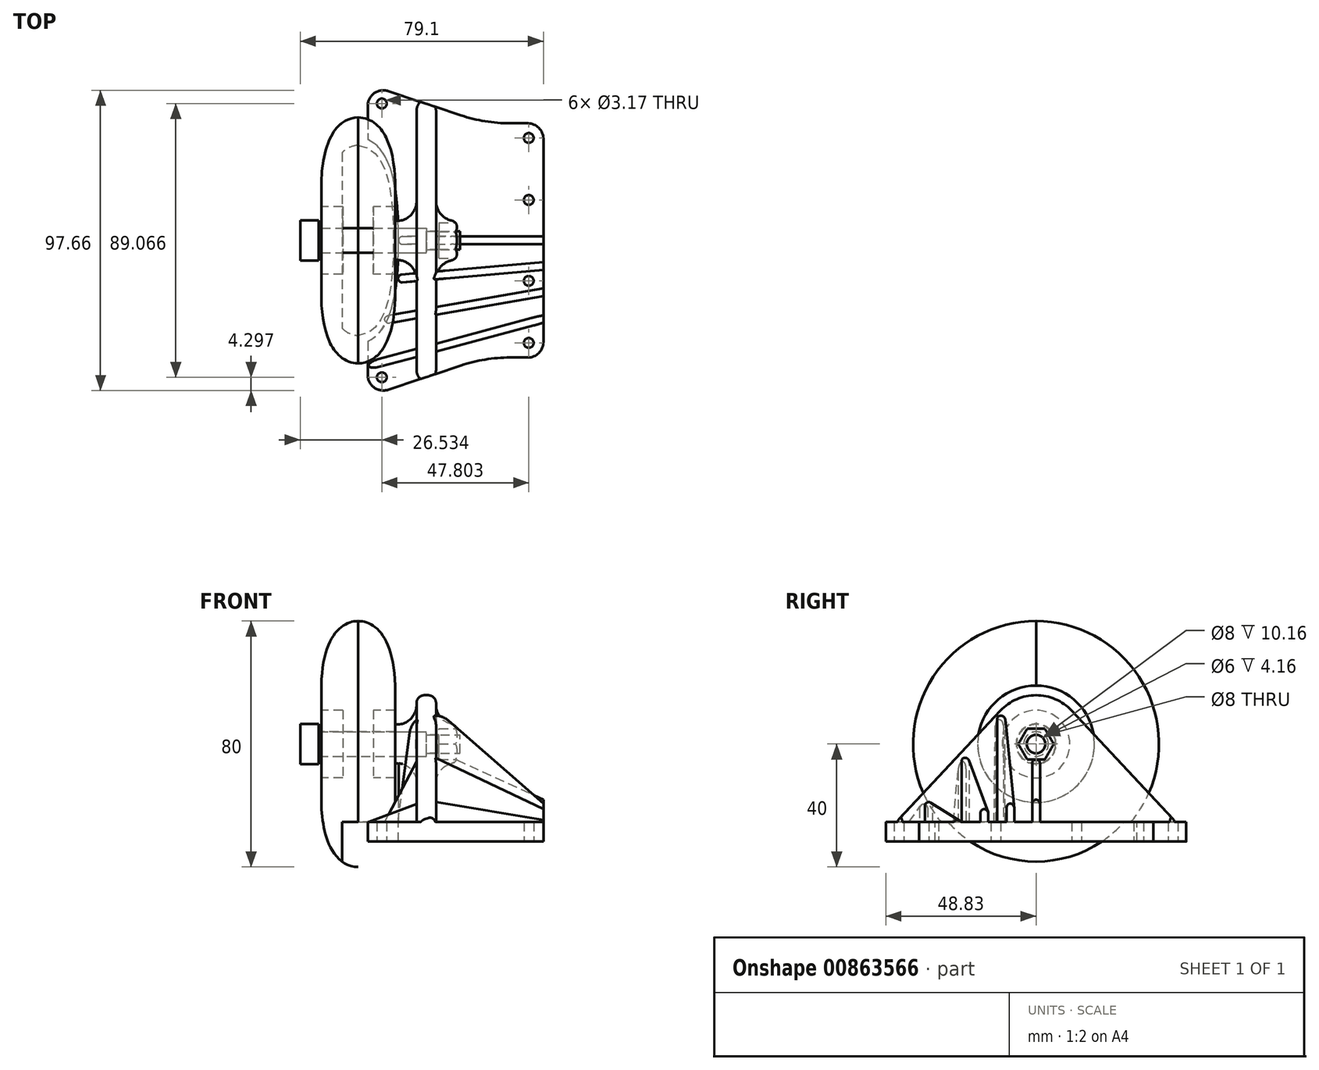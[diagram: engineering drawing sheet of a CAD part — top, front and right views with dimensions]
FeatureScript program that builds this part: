
annotation { "Feature Type Name" : "Feature", "Feature Type Description" : "" }
export const myFeature = defineFeature(function(context is Context, id is Id, definition is map)
    precondition{}
    {
        {
            var Q0;
            Q0=qCreatedBy(makeId("Top.planeOp"),FACE);
            var sketch = newSketch(context, id + "F0", { "sketchPlane" : qUnion([Q0])});
            skLineSegment(sketch, "E0", {"start": v(-19.05, 50.8) * mm, "end": v(-19.05, -50.8) * mm});
            skLineSegment(sketch, "E1", {"start": v(-19.05, -50.8) * mm, "end": v(19.05, -38.1) * mm});
            skLineSegment(sketch, "E2", {"start": v(38.1, -31.75) * mm, "end": v(38.1, 31.75) * mm});
            skLineSegment(sketch, "E3", {"start": v(19.05, 38.1) * mm, "end": v(-19.05, 50.8) * mm});
            skLineSegment(sketch, "E4", {"start": v(19.05, 38.1) * mm, "end": v(38.1, 38.1) * mm});
            skLineSegment(sketch, "E5", {"start": v(38.1, 38.1) * mm, "end": v(38.1, 31.75) * mm});
            skLineSegment(sketch, "E6", {"start": v(19.05, -38.1) * mm, "end": v(38.1, -38.1) * mm});
            skLineSegment(sketch, "E7", {"start": v(38.1, -38.1) * mm, "end": v(38.1, -31.75) * mm});
            skSolve(sketch);
        }
        {
            var Q0;
            Q0=makeQuery(id+"F0.imprint","IMPRINT",FACE,{"disambiguationData":[TD([[makeQuery(id+"F0.imprint","IMPRINT",EDGE,{"derivedFrom":sQuery(id+"F0.wireOp",EDGE,"E0")}),1.0]])]});
            extrude(context, id + "F1", {"entities" : qUnion([Q0]), "depth" : 6.35 * mm});
        }
        {
            var Q0;
            Q0=makeQuery(id+"F1.opExtrude","CAP_FACE",FACE,{"disambiguationData":[OSD([sQuery(id+"F0.wireOp",EDGE,"E0"),sQuery(id+"F0.wireOp",EDGE,"E1"),sQuery(id+"F0.wireOp",EDGE,"E2"),sQuery(id+"F0.wireOp",EDGE,"E3")])],"isStart":false});
            var sketch = newSketch(context, id + "F2", { "sketchPlane" : qUnion([Q0])});
            skLineSegment(sketch, "E8", {"start": v(-3.18, 45.5) * mm, "end": v(-3.17, -45.5) * mm});
            skLineSegment(sketch, "E9", {"start": v(-3.17, -45.5) * mm, "end": v(3.18, -43.4) * mm});
            skLineSegment(sketch, "E10", {"start": v(3.18, -43.4) * mm, "end": v(3.17, 43.4) * mm});
            skLineSegment(sketch, "E11", {"start": v(3.17, 43.4) * mm, "end": v(-3.18, 45.5) * mm});
            skSolve(sketch);
        }
        {
            var Q0;
            Q0=makeQuery(id+"F2.imprint","IMPRINT",FACE,{"disambiguationData":[TD([[makeQuery(id+"F2.imprint","IMPRINT",EDGE,{"derivedFrom":sQuery(id+"F2.wireOp",EDGE,"E8")}),1.0]])]});
            extrude(context, id + "F3", {"entities" : qUnion([Q0]), "operationType" : NewBodyOperationType.ADD, "depth" : 50.8 * mm, "offsetDistance" : 25.4 * mm});
        }
        {
            var Q0;
            Q0=qCreatedBy(makeId("Right.planeOp"),FACE);
            var sketch = newSketch(context, id + "F4", { "sketchPlane" : qUnion([Q0])});
            skArc(sketch, "E12", {"start": v(11.6, 42.6) * mm, "mid": v(0, 47.62) * mm, "end": v(-11.6, 42.6) * mm});
            skLineSegment(sketch, "E13", {"start": v(11.6, 42.6) * mm, "end": v(45.5, 6.35) * mm});
            skLineSegment(sketch, "E14", {"start": v(-11.6, 42.6) * mm, "end": v(-45.5, 6.35) * mm});
            skLineSegment(sketch, "E15", {"start": v(45.5, 6.35) * mm, "end": v(53.44, 6.35) * mm});
            skLineSegment(sketch, "E16", {"start": v(53.44, 6.35) * mm, "end": v(53.44, 59.99) * mm});
            skLineSegment(sketch, "E17", {"start": v(53.44, 59.99) * mm, "end": v(-55.67, 59.99) * mm});
            skLineSegment(sketch, "E18", {"start": v(-55.67, 59.99) * mm, "end": v(-55.67, 6.35) * mm});
            skLineSegment(sketch, "E19", {"start": v(-55.67, 6.35) * mm, "end": v(-45.5, 6.35) * mm});
            skSolve(sketch);
        }
        {
            var Q0;
            Q0=makeQuery(id+"F4.imprint","IMPRINT",FACE,{"disambiguationData":[TD([[makeQuery(id+"F4.imprint","IMPRINT",EDGE,{"derivedFrom":sQuery(id+"F4.wireOp",EDGE,"E12")}),-1.0]])]});
            extrude(context, id + "F5", {"entities" : qUnion([Q0]), "operationType" : NewBodyOperationType.REMOVE, "oppositeDirection" : true, "depth" : 7.11 * mm, "hasSecondDirection" : true, "secondDirectionOppositeDirection" : false, "secondDirectionDepth" : 4.06 * mm});
        }
        {
            var Q0;
            Q0=qCreatedBy(makeId("Right.planeOp"),FACE);
            var sketch = newSketch(context, id + "F6", { "sketchPlane" : qUnion([Q0])});
            skCircle(sketch, "E20", {"center": v(0, 513) * mm, "radius": 63.5 * mm});
            skCircle(sketch, "E21", {"center": v(0, 31.75) * mm, "radius": 6.35 * mm});
            skSolve(sketch);
        }
        {
            var Q0;
            Q0=qSketchRegion(id+"F6",true);
            extrude(context, id + "F7", {"entities" : qUnion([Q0]), "operationType" : NewBodyOperationType.ADD, "depth" : 10.16 * mm, "hasSecondDirection" : true, "secondDirectionOppositeDirection" : true, "secondDirectionDepth" : 10.16 * mm});
        }
        {
            var Q0;
            Q0=makeQuery(id+"F7.boolean.opBoolean","INTERSECT",EDGE,{"derivedFrom":[makeQuery(id+"F3.opExtrude","SWEPT_FACE",FACE,{"disambiguationData":[OSD([sQuery(id+"F2.wireOp",EDGE,"E8")])]}),makeQuery(id+"F7.opExtrude","SWEPT_FACE",FACE,{"disambiguationData":[OSD([sQuery(id+"F6.wireOp",EDGE,"E21")])]})]});
            var Q1;
            Q1=makeQuery(id+"F7.boolean.opBoolean","INTERSECT",EDGE,{"derivedFrom":[makeQuery(id+"F3.opExtrude","SWEPT_FACE",FACE,{"disambiguationData":[OSD([sQuery(id+"F2.wireOp",EDGE,"E10")])]}),makeQuery(id+"F7.opExtrude","SWEPT_FACE",FACE,{"disambiguationData":[OSD([sQuery(id+"F6.wireOp",EDGE,"E21")])]})]});
            fillet(context, id + "F8", {"entities" : qUnion([Q0, Q1]), "radius" : 6.35 * mm, "tangentPropagation" : true, "allowEdgeOverflow" : false});
        }
        {
            var Q0;
            Q0=makeQuery(id+"F5.boolean.opBoolean","INTERSECT",EDGE,{"derivedFrom":[makeQuery(id+"F3.opExtrude","SWEPT_FACE",FACE,{"disambiguationData":[OSD([sQuery(id+"F2.wireOp",EDGE,"E8")])]}),makeQuery(id+"F5.opExtrude","SWEPT_FACE",FACE,{"disambiguationData":[OSD([sQuery(id+"F4.wireOp",EDGE,"E13")])]})]});
            var Q1;
            Q1=makeQuery(id+"F5.boolean.opBoolean","INTERSECT",EDGE,{"derivedFrom":[makeQuery(id+"F3.opExtrude","SWEPT_FACE",FACE,{"disambiguationData":[OSD([sQuery(id+"F2.wireOp",EDGE,"E10")])]}),makeQuery(id+"F5.opExtrude","SWEPT_FACE",FACE,{"disambiguationData":[OSD([sQuery(id+"F4.wireOp",EDGE,"E13")])]})]});
            fillet(context, id + "F9", {"entities" : qUnion([Q0, Q1]), "radius" : 2.54 * mm, "tangentPropagation" : true, "allowEdgeOverflow" : false});
        }
        {
            var Q0;
            Q0=qCreatedBy(makeId("Right.planeOp"),FACE);
            var sketch = newSketch(context, id + "F10", { "sketchPlane" : qUnion([Q0])});
            skCircle(sketch, "E22", {"center": v(0, 31.75) * mm, "radius": 4 * mm});
            skSolve(sketch);
        }
        {
            var Q0;
            Q0=qSketchRegion(id+"F10",true);
            extrude(context, id + "F11", {"entities" : qUnion([Q0]), "operationType" : NewBodyOperationType.REMOVE, "oppositeDirection" : true, "depth" : 25.4 * mm});
        }
        {
            var Q0;
            Q0=makeQuery(id+"F7.opExtrude","CAP_FACE",FACE,{"disambiguationData":[OSD([sQuery(id+"F6.wireOp",EDGE,"E21")])],"isStart":false});
            var sketch = newSketch(context, id + "F12", { "sketchPlane" : qUnion([Q0])});
            skCircle(sketch, "E23.cCircle", {"center": v(0, 31.75) * mm, "radius": 5 * mm, "construction": true});
            skLineSegment(sketch, "E23.0", {"start": v(-2.89, 36.75) * mm, "end": v(2.89, 36.75) * mm});
            skLineSegment(sketch, "E23.1", {"start": v(2.89, 36.75) * mm, "end": v(5.77, 31.75) * mm});
            skLineSegment(sketch, "E23.2", {"start": v(5.77, 31.75) * mm, "end": v(2.89, 26.75) * mm});
            skLineSegment(sketch, "E23.3", {"start": v(2.89, 26.75) * mm, "end": v(-2.89, 26.75) * mm});
            skLineSegment(sketch, "E23.4", {"start": v(-2.89, 26.75) * mm, "end": v(-5.77, 31.75) * mm});
            skLineSegment(sketch, "E23.5", {"start": v(-5.77, 31.75) * mm, "end": v(-2.89, 36.75) * mm});
            skPoint(sketch, "E23.0.midPoint", {"position": v(0, 36.75) * mm});
            skSolve(sketch);
        }
        {
            var Q0;
            Q0=makeQuery(id+"F12.imprint","IMPRINT",FACE,{"disambiguationData":[TD([[makeQuery(id+"F12.imprint","IMPRINT",EDGE,{"derivedFrom":sQuery(id+"F12.wireOp",EDGE,"E23.0")}),-1.0]])]});
            extrude(context, id + "F13", {"entities" : qUnion([Q0]), "operationType" : NewBodyOperationType.REMOVE, "oppositeDirection" : true, "depth" : 6 * mm});
        }
        {
            var Q0;
            Q0=makeQuery(id+"F7.opExtrude","CAP_EDGE",EDGE,{"disambiguationData":[OSD([sQuery(id+"F6.wireOp",EDGE,"E21")])],"isStart":false});
            fillet(context, id + "F14", {"entities" : qUnion([Q0]), "radius" : 2.54 * mm, "tangentPropagation" : true, "allowEdgeOverflow" : false});
        }
        {
            var Q0;
            Q0=makeQuery(id+"F7.opExtrude","SWEPT_BODY",BODY,{"disambiguationData":[OSD([sQuery(id+"F6.wireOp",EDGE,"E20")])]});
            deleteBodies(context, id + "F15", {"entities" : qUnion([Q0])});
        }
        {
            var Q0;
            Q0=qCreatedBy(makeId("Right.planeOp"),FACE);
            var sketch = newSketch(context, id + "F16", { "sketchPlane" : qUnion([Q0])});
            skCircle(sketch, "E24", {"center": v(0, 31.75) * mm, "radius": 3 * mm});
            skSolve(sketch);
        }
        {
            var Q0;
            Q0=qSketchRegion(id+"F16",true);
            extrude(context, id + "F17", {"entities" : qUnion([Q0]), "operationType" : NewBodyOperationType.REMOVE, "depth" : 25.4 * mm});
        }
        {
            var Q0;
            Q0=qCreatedBy(makeId("Front.planeOp"),FACE);
            var sketch = newSketch(context, id + "F18", { "sketchPlane" : qUnion([Q0])});
            skLineSegment(sketch, "E25", {"start": v(0, 31.75) * mm, "end": v(-46.53, 31.75) * mm, "construction": true});
            skLineSegment(sketch, "E26", {"start": v(-35, 35.75) * mm, "end": v(0, 35.75) * mm});
            skLineSegment(sketch, "E27", {"start": v(0, 35.75) * mm, "end": v(0, 34.75) * mm});
            skLineSegment(sketch, "E28", {"start": v(0, 34.75) * mm, "end": v(11, 34.75) * mm});
            skLineSegment(sketch, "E29", {"start": v(11, 34.75) * mm, "end": v(11, 31.75) * mm});
            skLineSegment(sketch, "E30", {"start": v(11, 31.75) * mm, "end": v(-41, 31.75) * mm});
            skLineSegment(sketch, "E31", {"start": v(-35, 35.75) * mm, "end": v(-35, 38.25) * mm});
            skLineSegment(sketch, "E32", {"start": v(-35, 38.25) * mm, "end": v(-41, 38.25) * mm});
            skLineSegment(sketch, "E33", {"start": v(-41, 38.25) * mm, "end": v(-41, 31.75) * mm});
            skSolve(sketch);
        }
        {
            var Q0;
            Q0=makeQuery(id+"F18.imprint","IMPRINT",FACE,{"disambiguationData":[TD([[makeQuery(id+"F18.imprint","IMPRINT",EDGE,{"derivedFrom":sQuery(id+"F18.wireOp",EDGE,"E26")}),-1.0]])]});
            var Q1;
            Q1=sQuery(id+"F18.wireOp",EDGE,"E25");
            revolve(context, id + "F19", {"entities" : qUnion([Q0]), "axis" : qUnion([Q1]), "revolveType" : RevolveType.FULL});
        }
        {
            var Q0;
            Q0=qCreatedBy(makeId("Front.planeOp"),FACE);
            var sketch = newSketch(context, id + "F20", { "sketchPlane" : qUnion([Q0])});
            skLineSegment(sketch, "E34", {"start": v(-51.26, 31.75) * mm, "end": v(0, 31.75) * mm});
            skLineSegment(sketch, "E35", {"start": v(-22.16, 31.75) * mm, "end": v(-22.16, 71.75) * mm, "construction": true});
            skPoint(sketch, "E36", {"position": v(-25.63, 31.75) * mm});
            skLineSegment(sketch, "E37", {"start": v(-22.16, 35.75) * mm, "end": v(-10.16, 35.75) * mm});
            skLineSegment(sketch, "E38", {"start": v(-10.16, 35.75) * mm, "end": v(-10.16, 50.75) * mm});
            skPoint(sketch, "E39.MirrorCS.2.internal.orphan", {"position": v(-34.16, 31.75) * mm});
            skPoint(sketch, "E39.MirrorCS.start.orphan", {"position": v(-22.16, 71.75) * mm});
            skPoint(sketch, "E40.2.internal.orphan", {"position": v(-10.16, 31.75) * mm});
            skFitSpline(sketch, "E41", {"points": [v(-22.16, 71.75) * mm, v(-10.16, 50.75) * mm], "startDerivative": vector(15.26, -0.07) * mm, "endDerivative": vector(1.21, -49.43) * mm});
            skPoint(sketch, "E42.MirrorCS.end.orphan", {"position": v(-34.16, 50.75) * mm});
            skFitSpline(sketch, "E43.MirrorCS", {"points": [v(-22.16, 71.75) * mm, v(-34.16, 50.75) * mm], "startDerivative": vector(-15.26, -0.07) * mm, "endDerivative": vector(-1.21, -49.43) * mm});
            skLineSegment(sketch, "E44.MirrorCS", {"start": v(-34.16, 35.75) * mm, "end": v(-34.16, 50.75) * mm});
            skLineSegment(sketch, "E45.MirrorCS", {"start": v(-22.16, 35.75) * mm, "end": v(-34.16, 35.75) * mm});
            skSolve(sketch);
        }
        {
            var Q0;
            Q0=makeQuery(id+"F20.imprint","IMPRINT",FACE,{"disambiguationData":[TD([[makeQuery(id+"F20.imprint","IMPRINT",EDGE,{"derivedFrom":sQuery(id+"F20.wireOp",EDGE,"E37")}),1.0]])]});
            var Q1;
            Q1=sQuery(id+"F20.wireOp",EDGE,"E34");
            revolve(context, id + "F21", {"entities" : qUnion([Q0]), "axis" : qUnion([Q1]), "revolveType" : RevolveType.FULL});
        }
        {
            var Q0;
            Q0=qCreatedBy(makeId("Front.planeOp"),FACE);
            var sketch = newSketch(context, id + "F22", { "sketchPlane" : qUnion([Q0])});
            skLineSegment(sketch, "E46", {"start": v(-62.06, 31.75) * mm, "end": v(0, 31.75) * mm, "construction": true});
            skLineSegment(sketch, "E47", {"start": v(-10.16, 31.75) * mm, "end": v(-10.16, 42.75) * mm});
            skLineSegment(sketch, "E48", {"start": v(-10.16, 42.75) * mm, "end": v(-17.16, 42.75) * mm});
            skLineSegment(sketch, "E49", {"start": v(-17.16, 42.75) * mm, "end": v(-17.16, 31.75) * mm});
            skLineSegment(sketch, "E50", {"start": v(-17.16, 31.75) * mm, "end": v(-10.16, 31.75) * mm});
            skLineSegment(sketch, "E51", {"start": v(-22.16, 31.75) * mm, "end": v(-22.16, 46.12) * mm, "construction": true});
            skLineSegment(sketch, "E52.MirrorCS", {"start": v(-34.16, 42.75) * mm, "end": v(-27.16, 42.75) * mm});
            skLineSegment(sketch, "E53.MirrorCS", {"start": v(-27.16, 42.75) * mm, "end": v(-27.16, 31.75) * mm});
            skLineSegment(sketch, "E54.MirrorCS", {"start": v(-34.16, 31.75) * mm, "end": v(-34.16, 42.75) * mm});
            skLineSegment(sketch, "E55", {"start": v(-27.16, 31.75) * mm, "end": v(-34.16, 31.75) * mm});
            skSolve(sketch);
        }
        {
            var Q0;
            Q0=qSketchRegion(id+"F22",true);
            var Q1;
            Q1=sQuery(id+"F22.wireOp",EDGE,"E46");
            revolve(context, id + "F23", {"entities" : qUnion([Q0]), "axis" : qUnion([Q1]), "revolveType" : RevolveType.FULL});
        }
        {
            var Q0;
            {var subQ0=sQuery(id+"F0.wireOp",EDGE,"E3");var subQ1=sQuery(id+"F0.wireOp",EDGE,"E1");var subQ2=sQuery(id+"F0.wireOp",EDGE,"E0");Q0=makeQuery(id+"F3.boolean.opBoolean","SPLIT",FACE,{"disambiguationData":[TD([makeQuery(id+"F1.opExtrude","SWEPT_FACE",FACE,{"disambiguationData":[OSD([subQ2])]})])],"derivedFrom":makeQuery(id+"F1.opExtrude","CAP_FACE",FACE,{"disambiguationData":[OSD([subQ2,subQ1,sQuery(id+"F0.wireOp",EDGE,"E2"),subQ0])],"isStart":false})});}
            var sketch = newSketch(context, id + "F24", { "sketchPlane" : qUnion([Q0])});
            skLineSegment(sketch, "E56", {"start": v(-19.05, 32.85) * mm, "end": v(-19.05, -32.85) * mm});
            skFitSpline(sketch, "E57.0", {"points": [v(-22.67, -33.39) * mm, v(-22.46, -33.43) * mm, v(-22.05, -33.49) * mm, v(-21.48, -33.49) * mm, v(-20.97, -33.44) * mm, v(-20.5, -33.35) * mm, v(-20.07, -33.24) * mm, v(-19.65, -33.1) * mm, v(-19.27, -32.95) * mm, v(-18.9, -32.79) * mm, v(-18.56, -32.62) * mm, v(-18.23, -32.43) * mm, v(-17.91, -32.24) * mm, v(-17.5, -31.97) * mm, v(-17.03, -31.62) * mm, v(-16.3, -31.03) * mm, v(-15.49, -30.22) * mm, v(-14.62, -29.2) * mm, v(-13.87, -28.1) * mm, v(-13.21, -26.98) * mm, v(-12.65, -25.84) * mm, v(-12.17, -24.7) * mm, v(-11.76, -23.55) * mm, v(-11.28, -22.02) * mm, v(-10.8, -20.12) * mm, v(-10.34, -17.83) * mm, v(-10, -15.56) * mm, v(-9.63, -12.57) * mm, v(-9.33, -8.85) * mm, v(-9.13, -4.4) * mm, v(-9.07, 0.02) * mm, v(-9.13, 4.46) * mm, v(-9.3, 8.17) * mm, v(-9.52, 11.16) * mm, v(-9.73, 13.4) * mm, v(-10, 15.66) * mm, v(-10.36, 17.92) * mm, v(-10.81, 20.2) * mm, v(-11.4, 22.47) * mm, v(-12.03, 24.37) * mm, v(-12.67, 25.89) * mm, v(-13.24, 27.03) * mm, v(-13.9, 28.15) * mm, v(-14.65, 29.23) * mm, v(-15.52, 30.26) * mm, v(-16.5, 31.2) * mm, v(-17.6, 32.06) * mm, v(-18.66, 32.7) * mm, v(-19.65, 33.11) * mm, v(-20.35, 33.32) * mm, v(-20.98, 33.44) * mm, v(-21.49, 33.49) * mm, v(-22.05, 33.48) * mm, v(-22.46, 33.43) * mm, v(-22.67, 33.39) * mm]});
            skPoint(sketch, "E58.trimOffspring.end.orphan", {"position": v(-22.16, 30.9) * mm});
            skPoint(sketch, "E59.start.orphan", {"position": v(-22.16, -30.9) * mm});
            skLineSegment(sketch, "E60", {"start": v(-19.05, 32.85) * mm, "end": v(-27.36, 32.85) * mm});
            skLineSegment(sketch, "E61", {"start": v(-27.36, 32.85) * mm, "end": v(-27.36, -33.81) * mm});
            skLineSegment(sketch, "E62", {"start": v(-27.36, -33.81) * mm, "end": v(-19.05, -32.85) * mm});
            skSolve(sketch);
        }
        {
            var Q0;
            Q0=makeQuery(id+"F24.imprint","IMPRINT",FACE,{"disambiguationData":[TD([[makeQuery(id+"F24.imprint","IMPRINT",EDGE,{"derivedFrom":sQuery(id+"F24.wireOp",EDGE,"E56")}),-1.0]])]});
            var Q1;
            Q1=makeQuery(id+"F24.imprint","IMPRINT",FACE,{"disambiguationData":[TD([[makeQuery(id+"F24.imprint","IMPRINT",EDGE,{"derivedFrom":sQuery(id+"F24.wireOp",EDGE,"E56")}),1.0]])]});
            extrude(context, id + "F25", {"entities" : qUnion([Q0, Q1]), "operationType" : NewBodyOperationType.REMOVE, "oppositeDirection" : true, "depth" : 25.4 * mm});
        }
        {
            var Q0;
            Q0=qCreatedBy(makeId("Front.planeOp"),FACE);
            var sketch = newSketch(context, id + "F26", { "sketchPlane" : qUnion([Q0])});
            skLineSegment(sketch, "E63", {"start": v(-9.01, 6.35) * mm, "end": v(-9.01, 26.67) * mm});
            skLineSegment(sketch, "E64", {"start": v(-9.01, 26.67) * mm, "end": v(9.85, 26.67) * mm});
            skLineSegment(sketch, "E65", {"start": v(9.85, 26.67) * mm, "end": v(53.98, 6.35) * mm});
            skLineSegment(sketch, "E66", {"start": v(53.98, 6.35) * mm, "end": v(-9.01, 6.35) * mm});
            skSolve(sketch);
        }
        {
            var Q0;
            Q0=makeQuery(id+"F26.imprint","IMPRINT",FACE,{"disambiguationData":[TD([[makeQuery(id+"F26.imprint","IMPRINT",EDGE,{"derivedFrom":sQuery(id+"F26.wireOp",EDGE,"E63")}),-1.0]])]});
            extrude(context, id + "F27", {"entities" : qUnion([Q0]), "operationType" : NewBodyOperationType.ADD, "depth" : 1.27 * mm, "hasSecondDirection" : true, "secondDirectionOppositeDirection" : true, "secondDirectionDepth" : 1.27 * mm});
        }
        {
            var Q0;
            Q0=qCreatedBy(makeId("Top.planeOp"),FACE);
            var sketch = newSketch(context, id + "F28", { "sketchPlane" : qUnion([Q0])});
            skLineSegment(sketch, "E67", {"start": v(-23.06, -52.14) * mm, "end": v(133.35, 0) * mm});
            skLineSegment(sketch, "E68", {"start": v(133.35, 0) * mm, "end": v(-28.84, 0) * mm});
            skLineSegment(sketch, "E69", {"start": v(133.35, 0) * mm, "end": v(-37.86, -14.98) * mm});
            skLineSegment(sketch, "E70", {"start": v(133.35, 0) * mm, "end": v(-37.54, -30.13) * mm});
            skLineSegment(sketch, "E71", {"start": v(133.35, 0) * mm, "end": v(-45.99, -48.05) * mm});
            skSolve(sketch);
        }
        {
            var Q0;
            Q0=sQuery(id+"F28.wireOp",EDGE,"E69");
            cPlane(context, id + "F29", {"entities" : qUnion([Q0]), "cplaneType" : CPlaneType.LINE_ANGLE, "offset" : 25.4 * mm, "angle" : 0 * degree, "width" : 152.4 * mm, "height" : 152.4 * mm});
        }
        {
            var Q0;
            Q0=qCreatedBy(id+"F29.planeOp",FACE);
            var sketch = newSketch(context, id + "F30", { "sketchPlane" : qUnion([Q0])});
            skLineSegment(sketch, "E72", {"start": v(6.12, 39.44) * mm, "end": v(44.18, 6.35) * mm});
            skLineSegment(sketch, "E73", {"start": v(44.18, 6.35) * mm, "end": v(-10.24, 6.35) * mm});
            skLineSegment(sketch, "E74", {"start": v(-10.24, 6.35) * mm, "end": v(-6.43, 35.5) * mm});
            skPoint(sketch, "E75.visualSharp", {"position": v(-6.52, 34.82) * mm});
            skArc(sketch, "E75.filletArc", {"start": v(-3.16, 40.25) * mm, "mid": v(-5.37, 38.27) * mm, "end": v(-6.43, 35.5) * mm});
            skLineSegment(sketch, "E76", {"start": v(1.95, 41) * mm, "end": v(0.46, 41) * mm});
            skLineSegment(sketch, "E77", {"start": v(0.46, 41) * mm, "end": v(-3.16, 40.25) * mm});
            skPoint(sketch, "E78.visualSharp", {"position": v(4.32, 41) * mm});
            skArc(sketch, "E78.filletArc", {"start": v(6.12, 39.44) * mm, "mid": v(4.17, 40.6) * mm, "end": v(1.95, 41) * mm});
            skSolve(sketch);
        }
        {
            var Q0;
            Q0=makeQuery(id+"F30.imprint","IMPRINT",FACE,{"disambiguationData":[TD([[makeQuery(id+"F30.imprint","IMPRINT",EDGE,{"derivedFrom":sQuery(id+"F30.wireOp",EDGE,"E72")}),-1.0]])]});
            extrude(context, id + "F31", {"entities" : qUnion([Q0]), "operationType" : NewBodyOperationType.ADD, "depth" : 1.27 * mm, "hasSecondDirection" : true, "secondDirectionOppositeDirection" : true, "secondDirectionDepth" : 1.27 * mm});
        }
        {
            var Q0;
            Q0=sQuery(id+"F28.wireOp",EDGE,"E70");
            cPlane(context, id + "F32", {"entities" : qUnion([Q0]), "cplaneType" : CPlaneType.LINE_ANGLE, "offset" : 25.4 * mm, "angle" : 0 * degree, "width" : 152.4 * mm, "height" : 152.4 * mm});
        }
        {
            var Q0;
            Q0=qCreatedBy(id+"F32.planeOp",FACE);
            var sketch = newSketch(context, id + "F33", { "sketchPlane" : qUnion([Q0])});
            skLineSegment(sketch, "E79", {"start": v(43.53, 6.35) * mm, "end": v(-17.77, 6.35) * mm});
            skLineSegment(sketch, "E80", {"start": v(-17.77, 6.35) * mm, "end": v(-6.14, 28.2) * mm});
            skLineSegment(sketch, "E81", {"start": v(-6.14, 28.2) * mm, "end": v(-2.9, 28.2) * mm});
            skLineSegment(sketch, "E82", {"start": v(-2.9, 28.2) * mm, "end": v(43.53, 6.35) * mm});
            skSolve(sketch);
        }
        {
            var Q0;
            Q0=makeQuery(id+"F33.imprint","IMPRINT",FACE,{"disambiguationData":[TD([[makeQuery(id+"F33.imprint","IMPRINT",EDGE,{"derivedFrom":sQuery(id+"F33.wireOp",EDGE,"E79")}),-1.0]])]});
            extrude(context, id + "F34", {"entities" : qUnion([Q0]), "operationType" : NewBodyOperationType.ADD, "depth" : 1.27 * mm, "hasSecondDirection" : true, "secondDirectionOppositeDirection" : true, "secondDirectionDepth" : 1.27 * mm});
        }
        {
            var Q0;
            Q0=sQuery(id+"F28.wireOp",EDGE,"E71");
            cPlane(context, id + "F35", {"entities" : qUnion([Q0]), "cplaneType" : CPlaneType.LINE_ANGLE, "offset" : 25.4 * mm, "angle" : 0 * degree, "width" : 152.4 * mm, "height" : 152.4 * mm});
        }
        {
            var Q0;
            Q0=qCreatedBy(id+"F35.planeOp",FACE);
            var sketch = newSketch(context, id + "F36", { "sketchPlane" : qUnion([Q0])});
            skLineSegment(sketch, "E83", {"start": v(-28.7, 6.35) * mm, "end": v(-10.05, 13.08) * mm});
            skLineSegment(sketch, "E84", {"start": v(-10.05, 13.08) * mm, "end": v(-7.43, 13.08) * mm});
            skLineSegment(sketch, "E85", {"start": v(-7.43, 13.08) * mm, "end": v(34.6, 6.35) * mm});
            skLineSegment(sketch, "E86", {"start": v(34.6, 6.35) * mm, "end": v(-28.7, 6.35) * mm});
            skSolve(sketch);
        }
        {
            var Q0;
            Q0=makeQuery(id+"F36.imprint","IMPRINT",FACE,{"disambiguationData":[TD([[makeQuery(id+"F36.imprint","IMPRINT",EDGE,{"derivedFrom":sQuery(id+"F36.wireOp",EDGE,"E83")}),-1.0]])]});
            extrude(context, id + "F37", {"entities" : qUnion([Q0]), "operationType" : NewBodyOperationType.ADD, "depth" : 1.27 * mm, "hasSecondDirection" : true, "secondDirectionOppositeDirection" : true, "secondDirectionDepth" : 1.27 * mm});
        }
        {
            var Q0;
            Q0=makeQuery(id+"F1.opExtrude","SWEPT_EDGE",EDGE,{"disambiguationData":[OSD([sQuery(id+"F0.wireOp",EDGE,"E0"),sQuery(id+"F0.wireOp",EDGE,"E3")])]});
            var Q1;
            Q1=makeQuery(id+"F1.opExtrude","SWEPT_EDGE",EDGE,{"disambiguationData":[OSD([sQuery(id+"F0.wireOp",EDGE,"E0"),sQuery(id+"F0.wireOp",EDGE,"E1")])]});
            fillet(context, id + "F38", {"entities" : qUnion([Q0, Q1]), "radius" : 5.08 * mm, "tangentPropagation" : true, "allowEdgeOverflow" : false});
        }
        {
            var Q0;
            Q0=qCreatedBy(makeId("Top.planeOp"),FACE);
            var sketch = newSketch(context, id + "F39", { "sketchPlane" : qUnion([Q0])});
            skCircle(sketch, "E87", {"center": v(-14.47, 44.53) * mm, "radius": 1.59 * mm});
            skCircle(sketch, "E88", {"center": v(33.34, 33.34) * mm, "radius": 1.59 * mm});
            skCircle(sketch, "E89", {"center": v(33.34, 13.15) * mm, "radius": 1.59 * mm});
            skLineSegment(sketch, "E90", {"start": v(-47.45, 0) * mm, "end": v(55.73, 0) * mm, "construction": true});
            skCircle(sketch, "E91.MirrorC", {"center": v(-14.47, -44.53) * mm, "radius": 1.59 * mm});
            skCircle(sketch, "E92.MirrorC", {"center": v(33.34, -33.34) * mm, "radius": 1.59 * mm});
            skCircle(sketch, "E93.MirrorC", {"center": v(33.34, -13.15) * mm, "radius": 1.59 * mm});
            skSolve(sketch);
        }
        {
            var Q0;
            Q0=qSketchRegion(id+"F39",true);
            extrude(context, id + "F40", {"entities" : qUnion([Q0]), "operationType" : NewBodyOperationType.REMOVE, "depth" : 25.4 * mm});
        }
        {
            var Q0;
            Q0=qCreatedBy(makeId("Top.planeOp"),FACE);
            var sketch = newSketch(context, id + "F41", { "sketchPlane" : qUnion([Q0])});
            skLineSegment(sketch, "E94", {"start": v(38.1, 38.22) * mm, "end": v(38.1, -45.48) * mm});
            skLineSegment(sketch, "E95", {"start": v(38.1, -45.48) * mm, "end": v(62.17, -45.48) * mm});
            skLineSegment(sketch, "E96", {"start": v(62.17, -45.48) * mm, "end": v(51.52, 37.8) * mm});
            skLineSegment(sketch, "E97", {"start": v(51.52, 37.8) * mm, "end": v(38.1, 38.22) * mm});
            skSolve(sketch);
        }
        {
            var Q0;
            Q0=makeQuery(id+"F41.imprint","IMPRINT",FACE,{"disambiguationData":[TD([[makeQuery(id+"F41.imprint","IMPRINT",EDGE,{"derivedFrom":sQuery(id+"F41.wireOp",EDGE,"E94")}),1.0]])]});
            extrude(context, id + "F42", {"entities" : qUnion([Q0]), "operationType" : NewBodyOperationType.REMOVE, "depth" : 22.35 * mm});
        }
        {
            var Q0;
            Q0=makeQuery(id+"F1.opExtrude","SWEPT_EDGE",EDGE,{"disambiguationData":[OSD([sQuery(id+"F0.wireOp",EDGE,"E6"),sQuery(id+"F0.wireOp",EDGE,"E7")])]});
            var Q1;
            Q1=makeQuery(id+"F1.opExtrude","SWEPT_EDGE",EDGE,{"disambiguationData":[OSD([sQuery(id+"F0.wireOp",EDGE,"E4"),sQuery(id+"F0.wireOp",EDGE,"E5")])]});
            fillet(context, id + "F43", {"entities" : qUnion([Q0, Q1]), "radius" : 5.08 * mm, "tangentPropagation" : true, "allowEdgeOverflow" : false});
        }
        {
            var Q0;
            Q0=makeQuery(id+"F1.opExtrude","SWEPT_EDGE",EDGE,{"disambiguationData":[OSD([sQuery(id+"F0.wireOp",EDGE,"E3"),sQuery(id+"F0.wireOp",EDGE,"E4")])]});
            var Q1;
            Q1=makeQuery(id+"F1.opExtrude","SWEPT_EDGE",EDGE,{"disambiguationData":[OSD([sQuery(id+"F0.wireOp",EDGE,"E1"),sQuery(id+"F0.wireOp",EDGE,"E6")])]});
            fillet(context, id + "F44", {"entities" : qUnion([Q0, Q1]), "radius" : 50.8 * mm, "tangentPropagation" : true, "allowEdgeOverflow" : false});
        }
        {
            var Q0;
            Q0=makeQuery(id+"F27.opExtrude","CAP_EDGE",EDGE,{"disambiguationData":[OSD([sQuery(id+"F26.wireOp",EDGE,"E65")])],"isStart":false});
            var Q1;
            Q1=makeQuery(id+"F27.opExtrude","CAP_EDGE",EDGE,{"disambiguationData":[OSD([sQuery(id+"F26.wireOp",EDGE,"E65")])],"isStart":true});
            var Q2;
            Q2=makeQuery(id+"F31.opExtrude","CAP_EDGE",EDGE,{"disambiguationData":[OSD([sQuery(id+"F30.wireOp",EDGE,"E72")])],"isStart":true});
            var Q3;
            Q3=makeQuery(id+"F31.opExtrude","CAP_EDGE",EDGE,{"disambiguationData":[OSD([sQuery(id+"F30.wireOp",EDGE,"E72")])],"isStart":false});
            var Q4;
            Q4=makeQuery(id+"F31.opExtrude","CAP_EDGE",EDGE,{"disambiguationData":[OSD([sQuery(id+"F30.wireOp",EDGE,"E75.filletArc")])],"isStart":false});
            var Q5;
            Q5=makeQuery(id+"F31.opExtrude","CAP_EDGE",EDGE,{"disambiguationData":[OSD([sQuery(id+"F30.wireOp",EDGE,"E75.filletArc")])],"isStart":true});
            var Q6;
            Q6=makeQuery(id+"F34.opExtrude","CAP_EDGE",EDGE,{"disambiguationData":[OSD([sQuery(id+"F33.wireOp",EDGE,"E82")])],"isStart":false});
            var Q7;
            Q7=makeQuery(id+"F34.opExtrude","CAP_EDGE",EDGE,{"disambiguationData":[OSD([sQuery(id+"F33.wireOp",EDGE,"E82")])],"isStart":true});
            var Q8;
            Q8=makeQuery(id+"F34.opExtrude","CAP_EDGE",EDGE,{"disambiguationData":[OSD([sQuery(id+"F33.wireOp",EDGE,"E80")])],"isStart":false});
            var Q9;
            Q9=makeQuery(id+"F34.opExtrude","CAP_EDGE",EDGE,{"disambiguationData":[OSD([sQuery(id+"F33.wireOp",EDGE,"E80")])],"isStart":true});
            var Q10;
            Q10=makeQuery(id+"F37.opExtrude","CAP_EDGE",EDGE,{"disambiguationData":[OSD([sQuery(id+"F36.wireOp",EDGE,"E83")])],"isStart":false});
            var Q11;
            Q11=makeQuery(id+"F37.opExtrude","CAP_EDGE",EDGE,{"disambiguationData":[OSD([sQuery(id+"F36.wireOp",EDGE,"E83")])],"isStart":true});
            var Q12;
            Q12=makeQuery(id+"F37.opExtrude","CAP_EDGE",EDGE,{"disambiguationData":[OSD([sQuery(id+"F36.wireOp",EDGE,"E85")])],"isStart":false});
            var Q13;
            Q13=makeQuery(id+"F37.opExtrude","CAP_EDGE",EDGE,{"disambiguationData":[OSD([sQuery(id+"F36.wireOp",EDGE,"E85")])],"isStart":true});
            var Q14;
            Q14=makeQuery(id+"FzpeDoiq8tc86xp_5.1.F31.opExtrude","CAP_EDGE",EDGE,{"disambiguationData":[OSD([sQuery(id+"F30.wireOp",EDGE,"E72")])],"isStart":true});
            var Q15;
            Q15=makeQuery(id+"FzpeDoiq8tc86xp_5.1.F31.opExtrude","CAP_EDGE",EDGE,{"disambiguationData":[OSD([sQuery(id+"F30.wireOp",EDGE,"E72")])],"isStart":false});
            var Q16;
            Q16=makeQuery(id+"FzpeDoiq8tc86xp_5.1.F34.opExtrude","CAP_EDGE",EDGE,{"disambiguationData":[OSD([sQuery(id+"F33.wireOp",EDGE,"E82")])],"isStart":true});
            var Q17;
            Q17=makeQuery(id+"FzpeDoiq8tc86xp_5.1.F34.opExtrude","CAP_EDGE",EDGE,{"disambiguationData":[OSD([sQuery(id+"F33.wireOp",EDGE,"E82")])],"isStart":false});
            var Q18;
            Q18=makeQuery(id+"FzpeDoiq8tc86xp_5.1.F37.opExtrude","CAP_EDGE",EDGE,{"disambiguationData":[OSD([sQuery(id+"F36.wireOp",EDGE,"E85")])],"isStart":true});
            var Q19;
            Q19=makeQuery(id+"FzpeDoiq8tc86xp_5.1.F37.opExtrude","CAP_EDGE",EDGE,{"disambiguationData":[OSD([sQuery(id+"F36.wireOp",EDGE,"E85")])],"isStart":false});
            var Q20;
            Q20=makeQuery(id+"F27.opExtrude","CAP_EDGE",EDGE,{"disambiguationData":[OSD([sQuery(id+"F26.wireOp",EDGE,"E63")])],"isStart":false});
            var Q21;
            Q21=makeQuery(id+"FzpeDoiq8tc86xp_5.1.F31.opExtrude","CAP_EDGE",EDGE,{"disambiguationData":[OSD([sQuery(id+"F30.wireOp",EDGE,"E74")])],"isStart":true});
            var Q22;
            Q22=makeQuery(id+"FzpeDoiq8tc86xp_5.1.F31.opExtrude","CAP_EDGE",EDGE,{"disambiguationData":[OSD([sQuery(id+"F30.wireOp",EDGE,"E74")])],"isStart":false});
            var Q23;
            Q23=makeQuery(id+"FzpeDoiq8tc86xp_5.1.F34.opExtrude","CAP_EDGE",EDGE,{"disambiguationData":[OSD([sQuery(id+"F33.wireOp",EDGE,"E80")])],"isStart":true});
            var Q24;
            Q24=makeQuery(id+"FzpeDoiq8tc86xp_5.1.F34.opExtrude","CAP_EDGE",EDGE,{"disambiguationData":[OSD([sQuery(id+"F33.wireOp",EDGE,"E80")])],"isStart":false});
            var Q25;
            Q25=makeQuery(id+"FzpeDoiq8tc86xp_5.1.F37.opExtrude","CAP_EDGE",EDGE,{"disambiguationData":[OSD([sQuery(id+"F36.wireOp",EDGE,"E83")])],"isStart":true});
            var Q26;
            Q26=makeQuery(id+"F27.opExtrude","CAP_EDGE",EDGE,{"disambiguationData":[OSD([sQuery(id+"F26.wireOp",EDGE,"E63")])],"isStart":true});
            fillet(context, id + "F45", {"entities" : qUnion([Q0, Q1, Q2, Q3, Q4, Q5, Q6, Q7, Q8, Q9, Q10, Q11, Q12, Q13, Q14, Q15, Q16, Q17, Q18, Q19, Q20, Q21, Q22, Q23, Q24, Q25, Q26]), "radius" : 1.27 * mm, "tangentPropagation" : true, "allowEdgeOverflow" : false});
        }
    });
